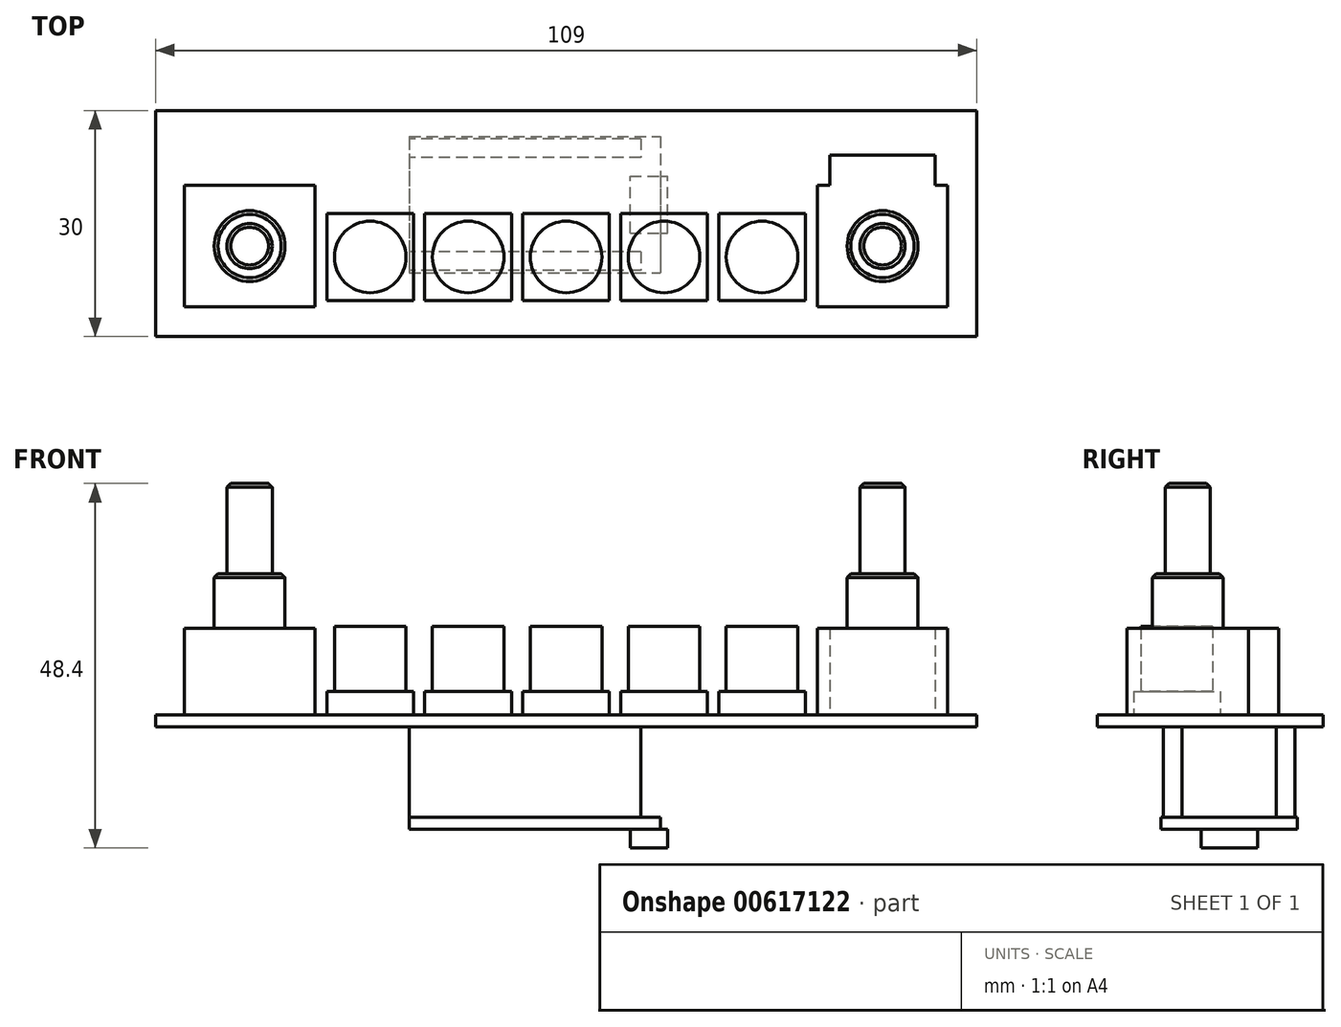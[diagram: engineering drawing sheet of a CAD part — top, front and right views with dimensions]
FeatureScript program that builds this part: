
annotation { "Feature Type Name" : "Feature", "Feature Type Description" : "" }
export const myFeature = defineFeature(function(context is Context, id is Id, definition is map)
    precondition{}
    {
        {
            var Q0;
            Q0=qCreatedBy(makeId("Top.planeOp"),FACE);
            var sketch = newSketch(context, id + "F0", { "sketchPlane" : qUnion([Q0])});
            skLineSegment(sketch, "E0.bottom", {"start": v(54.5, -15) * mm, "end": v(-54.5, -15) * mm});
            skLineSegment(sketch, "E0.top", {"start": v(54.5, 15) * mm, "end": v(-54.5, 15) * mm});
            skLineSegment(sketch, "E0.left", {"start": v(54.5, -15) * mm, "end": v(54.5, 15) * mm});
            skLineSegment(sketch, "E0.right", {"start": v(-54.5, -15) * mm, "end": v(-54.5, 15) * mm});
            skPoint(sketch, "E0.middle", {"position": v(0, 0) * mm});
            skLineSegment(sketch, "E1.bottom", {"start": v(-20.25, -10.2) * mm, "end": v(-31.75, -10.2) * mm});
            skLineSegment(sketch, "E1.top", {"start": v(-20.25, 1.3) * mm, "end": v(-31.75, 1.3) * mm});
            skLineSegment(sketch, "E1.left", {"start": v(-20.25, -10.2) * mm, "end": v(-20.25, 1.3) * mm});
            skLineSegment(sketch, "E1.right", {"start": v(-31.75, -10.2) * mm, "end": v(-31.75, 1.3) * mm});
            skPoint(sketch, "E1.middle", {"position": v(-26, -4.45) * mm});
            skLineSegment(sketch, "E2.1.0.0", {"start": v(-18.75, -10.2) * mm, "end": v(-18.75, 1.3) * mm});
            skLineSegment(sketch, "E2.1.0.1", {"start": v(-7.25, -10.2) * mm, "end": v(-7.25, 1.3) * mm});
            skLineSegment(sketch, "E2.1.0.2", {"start": v(-7.25, 1.3) * mm, "end": v(-18.75, 1.3) * mm});
            skPoint(sketch, "E2.1.0.3", {"position": v(-13, -4.45) * mm});
            skLineSegment(sketch, "E2.1.0.4", {"start": v(-7.25, -10.2) * mm, "end": v(-18.75, -10.2) * mm});
            skLineSegment(sketch, "E2.2.0.0", {"start": v(-5.75, -10.2) * mm, "end": v(-5.75, 1.3) * mm});
            skLineSegment(sketch, "E2.2.0.1", {"start": v(5.75, -10.2) * mm, "end": v(5.75, 1.3) * mm});
            skLineSegment(sketch, "E2.2.0.2", {"start": v(5.75, 1.3) * mm, "end": v(-5.75, 1.3) * mm});
            skPoint(sketch, "E2.2.0.3", {"position": v(0, -4.45) * mm});
            skLineSegment(sketch, "E2.2.0.4", {"start": v(5.75, -10.2) * mm, "end": v(-5.75, -10.2) * mm});
            skLineSegment(sketch, "E2.3.0.0", {"start": v(7.25, -10.2) * mm, "end": v(7.25, 1.3) * mm});
            skLineSegment(sketch, "E2.3.0.1", {"start": v(18.75, -10.2) * mm, "end": v(18.75, 1.3) * mm});
            skLineSegment(sketch, "E2.3.0.2", {"start": v(18.75, 1.3) * mm, "end": v(7.25, 1.3) * mm});
            skPoint(sketch, "E2.3.0.3", {"position": v(13, -4.45) * mm});
            skLineSegment(sketch, "E2.3.0.4", {"start": v(18.75, -10.2) * mm, "end": v(7.25, -10.2) * mm});
            skLineSegment(sketch, "E2.4.0.0", {"start": v(20.25, -10.2) * mm, "end": v(20.25, 1.3) * mm});
            skLineSegment(sketch, "E2.4.0.1", {"start": v(31.75, -10.2) * mm, "end": v(31.75, 1.3) * mm});
            skLineSegment(sketch, "E2.4.0.2", {"start": v(31.75, 1.3) * mm, "end": v(20.25, 1.3) * mm});
            skPoint(sketch, "E2.4.0.3", {"position": v(26, -4.45) * mm});
            skLineSegment(sketch, "E2.4.0.4", {"start": v(31.75, -10.2) * mm, "end": v(20.25, -10.2) * mm});
            skLineSegment(sketch, "E2.direction1", {"start": v(-31.75, -10.2) * mm, "end": v(-18.75, -10.2) * mm, "construction": true});
            skLineSegment(sketch, "E3", {"start": v(0, 21.15) * mm, "end": v(0, -24.83) * mm, "construction": true});
            skSolve(sketch);
        }
        {
            var Q0;
            Q0=makeQuery(id+"F0.imprint","IMPRINT",FACE,{"disambiguationData":[TD([[makeQuery(id+"F0.imprint","IMPRINT",EDGE,{"derivedFrom":sQuery(id+"F0.wireOp",EDGE,"E1.bottom")}),-1.0]])]});
            var Q1;
            Q1=makeQuery(id+"F0.imprint","IMPRINT",FACE,{"disambiguationData":[TD([[makeQuery(id+"F0.imprint","IMPRINT",EDGE,{"derivedFrom":sQuery(id+"F0.wireOp",EDGE,"E2.1.0.0")}),-1.0]])]});
            var Q2;
            Q2=makeQuery(id+"F0.imprint","IMPRINT",FACE,{"disambiguationData":[TD([[makeQuery(id+"F0.imprint","IMPRINT",EDGE,{"derivedFrom":sQuery(id+"F0.wireOp",EDGE,"E2.3.0.0")}),-1.0]])]});
            var Q3;
            Q3=makeQuery(id+"F0.imprint","IMPRINT",FACE,{"disambiguationData":[TD([[makeQuery(id+"F0.imprint","IMPRINT",EDGE,{"derivedFrom":sQuery(id+"F0.wireOp",EDGE,"E2.4.0.0")}),-1.0]])]});
            var Q4;
            Q4=makeQuery(id+"F0.imprint","IMPRINT",FACE,{"disambiguationData":[TD([[makeQuery(id+"F0.imprint","IMPRINT",EDGE,{"derivedFrom":sQuery(id+"F0.wireOp",EDGE,"E2.2.0.0")}),-1.0]])]});
            extrude(context, id + "F1", {"entities" : qUnion([Q0, Q1, Q2, Q3, Q4]), "depth" : 4.7 * mm, "offsetDistance" : 25 * mm});
        }
        {
            var Q0;
            Q0=makeQuery(id+"F0.imprint","IMPRINT",FACE,{"disambiguationData":[TD([[makeQuery(id+"F0.imprint","IMPRINT",EDGE,{"derivedFrom":sQuery(id+"F0.wireOp",EDGE,"E0.bottom")}),-1.0]])]});
            extrude(context, id + "F2", {"entities" : qUnion([Q0]), "operationType" : NewBodyOperationType.ADD, "depth" : 1.6 * mm, "offsetDistance" : 25 * mm});
        }
        {
            var Q0;
            Q0=makeQuery(id+"F1.opExtrude","CAP_FACE",FACE,{"disambiguationData":[OSD([sQuery(id+"F0.wireOp",EDGE,"E1.bottom"),sQuery(id+"F0.wireOp",EDGE,"E1.top"),sQuery(id+"F0.wireOp",EDGE,"E1.left"),sQuery(id+"F0.wireOp",EDGE,"E1.right")])],"isStart":false});
            var sketch = newSketch(context, id + "F3", { "sketchPlane" : qUnion([Q0])});
            skCircle(sketch, "E4", {"center": v(-26, -4.45) * mm, "radius": 4.75 * mm});
            skCircle(sketch, "E5.1.0.0", {"center": v(-13, -4.45) * mm, "radius": 4.75 * mm});
            skCircle(sketch, "E5.2.0.0", {"center": v(0, -4.45) * mm, "radius": 4.75 * mm});
            skCircle(sketch, "E5.3.0.0", {"center": v(13, -4.45) * mm, "radius": 4.75 * mm});
            skCircle(sketch, "E5.4.0.0", {"center": v(26, -4.45) * mm, "radius": 4.75 * mm});
            skLineSegment(sketch, "E5.direction1", {"start": v(-26, -4.45) * mm, "end": v(-13, -4.45) * mm, "construction": true});
            skSolve(sketch);
        }
        {
            var Q0;
            Q0=makeQuery(id+"F3.imprint","IMPRINT",FACE,{"disambiguationData":[TD([[makeQuery(id+"F3.imprint","IMPRINT",EDGE,{"derivedFrom":sQuery(id+"F3.wireOp",EDGE,"E4")}),1.0]])]});
            var Q1;
            Q1=makeQuery(id+"F3.imprint","IMPRINT",FACE,{"disambiguationData":[TD([[makeQuery(id+"F3.imprint","IMPRINT",EDGE,{"derivedFrom":sQuery(id+"F3.wireOp",EDGE,"E5.1.0.0")}),1.0]])]});
            var Q2;
            Q2=makeQuery(id+"F3.imprint","IMPRINT",FACE,{"disambiguationData":[TD([[makeQuery(id+"F3.imprint","IMPRINT",EDGE,{"derivedFrom":sQuery(id+"F3.wireOp",EDGE,"E5.2.0.0")}),1.0]])]});
            var Q3;
            Q3=makeQuery(id+"F3.imprint","IMPRINT",FACE,{"disambiguationData":[TD([[makeQuery(id+"F3.imprint","IMPRINT",EDGE,{"derivedFrom":sQuery(id+"F3.wireOp",EDGE,"E5.3.0.0")}),1.0]])]});
            var Q4;
            Q4=makeQuery(id+"F3.imprint","IMPRINT",FACE,{"disambiguationData":[TD([[makeQuery(id+"F3.imprint","IMPRINT",EDGE,{"derivedFrom":sQuery(id+"F3.wireOp",EDGE,"E5.4.0.0")}),1.0]])]});
            extrude(context, id + "F4", {"entities" : qUnion([Q0, Q1, Q2, Q3, Q4]), "operationType" : NewBodyOperationType.ADD, "depth" : 8.6 * mm, "offsetDistance" : 25 * mm});
        }
        {
            var Q0;
            Q0=makeQuery(id+"F2.opExtrude","CAP_FACE",FACE,{"disambiguationData":[OSD([sQuery(id+"F0.wireOp",EDGE,"E0.bottom"),sQuery(id+"F0.wireOp",EDGE,"E0.top"),sQuery(id+"F0.wireOp",EDGE,"E0.left"),sQuery(id+"F0.wireOp",EDGE,"E0.right"),sQuery(id+"F0.wireOp",EDGE,"E1.bottom"),sQuery(id+"F0.wireOp",EDGE,"E1.top"),sQuery(id+"F0.wireOp",EDGE,"E1.left"),sQuery(id+"F0.wireOp",EDGE,"E1.right"),sQuery(id+"F0.wireOp",EDGE,"E2.1.0.0"),sQuery(id+"F0.wireOp",EDGE,"E2.1.0.1"),sQuery(id+"F0.wireOp",EDGE,"E2.1.0.2"),sQuery(id+"F0.wireOp",EDGE,"E2.1.0.4"),sQuery(id+"F0.wireOp",EDGE,"E2.2.0.0"),sQuery(id+"F0.wireOp",EDGE,"E2.2.0.1"),sQuery(id+"F0.wireOp",EDGE,"E2.2.0.2"),sQuery(id+"F0.wireOp",EDGE,"E2.2.0.4"),sQuery(id+"F0.wireOp",EDGE,"E2.3.0.0"),sQuery(id+"F0.wireOp",EDGE,"E2.3.0.1"),sQuery(id+"F0.wireOp",EDGE,"E2.3.0.2"),sQuery(id+"F0.wireOp",EDGE,"E2.3.0.4"),sQuery(id+"F0.wireOp",EDGE,"E2.4.0.0"),sQuery(id+"F0.wireOp",EDGE,"E2.4.0.1"),sQuery(id+"F0.wireOp",EDGE,"E2.4.0.2"),sQuery(id+"F0.wireOp",EDGE,"E2.4.0.4")])],"isStart":false});
            var sketch = newSketch(context, id + "F5", { "sketchPlane" : qUnion([Q0])});
            skLineSegment(sketch, "E6.bottom", {"start": v(-33.35, -11.05) * mm, "end": v(-50.65, -11.05) * mm});
            skLineSegment(sketch, "E6.top", {"start": v(-33.35, 5.05) * mm, "end": v(-50.65, 5.05) * mm});
            skLineSegment(sketch, "E6.left", {"start": v(-33.35, -11.05) * mm, "end": v(-33.35, 5.05) * mm});
            skLineSegment(sketch, "E6.right", {"start": v(-50.65, -11.05) * mm, "end": v(-50.65, 5.05) * mm});
            skPoint(sketch, "E6.middle", {"position": v(-42, -3) * mm});
            skLineSegment(sketch, "E7.bottom", {"start": v(-35, 5.05) * mm, "end": v(-49, 5.05) * mm});
            skLineSegment(sketch, "E7.top", {"start": v(-35, 9.05) * mm, "end": v(-49, 9.05) * mm});
            skLineSegment(sketch, "E7.left", {"start": v(-35, 5.05) * mm, "end": v(-35, 9.05) * mm});
            skLineSegment(sketch, "E7.right", {"start": v(-49, 5.05) * mm, "end": v(-49, 9.05) * mm});
            skPoint(sketch, "E7.middle", {"position": v(-42, 7.05) * mm});
            skLineSegment(sketch, "E8", {"start": v(-39.97, -18.43) * mm, "end": v(-39.97, -18.43) * mm});
            skLineSegment(sketch, "E9", {"start": v(-42, -34.93) * mm, "end": v(-42, 23.71) * mm, "construction": true});
            skPoint(sketch, "E10.1.0.0", {"position": v(42, 7.05) * mm});
            skLineSegment(sketch, "E10.1.0.1", {"start": v(50.65, -11.05) * mm, "end": v(33.35, -11.05) * mm});
            skLineSegment(sketch, "E10.1.0.2", {"start": v(49, 9.05) * mm, "end": v(35, 9.05) * mm});
            skLineSegment(sketch, "E10.1.0.3", {"start": v(50.65, -11.05) * mm, "end": v(50.65, 5.05) * mm});
            skPoint(sketch, "E10.1.0.4", {"position": v(42, -3) * mm});
            skLineSegment(sketch, "E10.1.0.5", {"start": v(33.35, -11.05) * mm, "end": v(33.35, 5.05) * mm});
            skLineSegment(sketch, "E10.1.0.6", {"start": v(49, 5.05) * mm, "end": v(35, 5.05) * mm});
            skLineSegment(sketch, "E10.1.0.7", {"start": v(50.65, 5.05) * mm, "end": v(33.35, 5.05) * mm});
            skLineSegment(sketch, "E10.1.0.8", {"start": v(35, 5.05) * mm, "end": v(35, 9.05) * mm});
            skLineSegment(sketch, "E10.1.0.9", {"start": v(49, 5.05) * mm, "end": v(49, 9.05) * mm});
            skLineSegment(sketch, "E10.direction1", {"start": v(-50.65, -11.05) * mm, "end": v(33.35, -11.05) * mm, "construction": true});
            skSolve(sketch);
        }
        {
            var Q0;
            Q0=makeQuery(id+"F5.imprint","IMPRINT",FACE,{"disambiguationData":[TD([[makeQuery(id+"F5.imprint","IMPRINT",EDGE,{"derivedFrom":sQuery(id+"F5.wireOp",EDGE,"E6.bottom")}),-1.0]])]});
            var Q1;
            Q1=makeQuery(id+"F5.imprint","IMPRINT",FACE,{"disambiguationData":[TD([[makeQuery(id+"F5.imprint","IMPRINT",EDGE,{"derivedFrom":sQuery(id+"F5.wireOp",EDGE,"E7.bottom")}),-1.0]])]});
            var Q2;
            Q2=makeQuery(id+"F5.imprint","IMPRINT",FACE,{"disambiguationData":[TD([[makeQuery(id+"F5.imprint","IMPRINT",EDGE,{"derivedFrom":sQuery(id+"F5.wireOp",EDGE,"E10.1.0.2")}),1.0]])]});
            var Q3;
            Q3=makeQuery(id+"F5.imprint","IMPRINT",FACE,{"disambiguationData":[TD([[makeQuery(id+"F5.imprint","IMPRINT",EDGE,{"derivedFrom":sQuery(id+"F5.wireOp",EDGE,"E10.1.0.1")}),-1.0]])]});
            extrude(context, id + "F6", {"entities" : qUnion([Q0, Q1, Q2, Q3]), "operationType" : NewBodyOperationType.ADD, "depth" : 11.5 * mm, "offsetDistance" : 25 * mm});
        }
        {
            var Q0;
            Q0=makeQuery(id+"F6.opExtrude","CAP_FACE",FACE,{"disambiguationData":[OSD([sQuery(id+"F5.wireOp",EDGE,"E6.bottom"),sQuery(id+"F5.wireOp",EDGE,"E6.top"),sQuery(id+"F5.wireOp",EDGE,"E6.left"),sQuery(id+"F5.wireOp",EDGE,"E6.right"),sQuery(id+"F5.wireOp",EDGE,"E7.top"),sQuery(id+"F5.wireOp",EDGE,"E7.left"),sQuery(id+"F5.wireOp",EDGE,"E7.right")])],"isStart":false});
            var sketch = newSketch(context, id + "F7", { "sketchPlane" : qUnion([Q0])});
            skCircle(sketch, "E11", {"center": v(-42, -3) * mm, "radius": 4.7 * mm});
            skLineSegment(sketch, "E12", {"start": v(-50.65, -11.05) * mm, "end": v(-33.35, 5.05) * mm, "construction": true});
            skLineSegment(sketch, "E13", {"start": v(-50.65, 5.05) * mm, "end": v(-33.35, -11.05) * mm, "construction": true});
            skCircle(sketch, "E14.1.0.0", {"center": v(42, -3) * mm, "radius": 4.7 * mm});
            skLineSegment(sketch, "E14.direction1", {"start": v(-42, -3) * mm, "end": v(42, -3) * mm, "construction": true});
            skSolve(sketch);
        }
        {
            var Q0;
            Q0=makeQuery(id+"F7.imprint","IMPRINT",FACE,{"disambiguationData":[TD([[makeQuery(id+"F7.imprint","IMPRINT",EDGE,{"derivedFrom":sQuery(id+"F7.wireOp",EDGE,"E11")}),1.0]])]});
            var Q1;
            Q1=makeQuery(id+"F7.imprint","IMPRINT",FACE,{"disambiguationData":[TD([[makeQuery(id+"F7.imprint","IMPRINT",EDGE,{"derivedFrom":sQuery(id+"F7.wireOp",EDGE,"E14.1.0.0")}),1.0]])]});
            extrude(context, id + "F8", {"entities" : qUnion([Q0, Q1]), "operationType" : NewBodyOperationType.ADD, "depth" : 7.2 * mm, "offsetDistance" : 25 * mm});
        }
        {
            var Q0;
            Q0=makeQuery(id+"F8.opExtrude","CAP_FACE",FACE,{"disambiguationData":[OSD([sQuery(id+"F7.wireOp",EDGE,"E11")])],"isStart":false});
            var sketch = newSketch(context, id + "F9", { "sketchPlane" : qUnion([Q0])});
            skCircle(sketch, "E15", {"center": v(-42, -3) * mm, "radius": 3 * mm});
            skCircle(sketch, "E16.1.0.0", {"center": v(42, -3) * mm, "radius": 3 * mm});
            skLineSegment(sketch, "E16.direction1", {"start": v(-42, -3) * mm, "end": v(42, -3) * mm, "construction": true});
            skSolve(sketch);
        }
        {
            var Q0;
            Q0=makeQuery(id+"F9.imprint","IMPRINT",FACE,{"disambiguationData":[TD([[makeQuery(id+"F9.imprint","IMPRINT",EDGE,{"derivedFrom":sQuery(id+"F9.wireOp",EDGE,"E15")}),1.0]])]});
            var Q1;
            Q1=makeQuery(id+"F9.imprint","IMPRINT",FACE,{"disambiguationData":[TD([[makeQuery(id+"F9.imprint","IMPRINT",EDGE,{"derivedFrom":sQuery(id+"F9.wireOp",EDGE,"E16.1.0.0")}),1.0]])]});
            extrude(context, id + "F10", {"entities" : qUnion([Q0, Q1]), "operationType" : NewBodyOperationType.ADD, "depth" : 12 * mm, "offsetDistance" : 25 * mm});
        }
        {
            var Q0;
            Q0=makeQuery(id+"F8.opExtrude","CAP_EDGE",EDGE,{"disambiguationData":[OSD([sQuery(id+"F7.wireOp",EDGE,"E11")])],"isStart":false});
            var Q1;
            Q1=makeQuery(id+"F8.opExtrude","CAP_EDGE",EDGE,{"disambiguationData":[OSD([sQuery(id+"F7.wireOp",EDGE,"E14.1.0.0")])],"isStart":false});
            var Q2;
            Q2=makeQuery(id+"F10.opExtrude","CAP_EDGE",EDGE,{"disambiguationData":[OSD([sQuery(id+"F9.wireOp",EDGE,"E15")])],"isStart":false});
            var Q3;
            Q3=makeQuery(id+"F10.opExtrude","CAP_EDGE",EDGE,{"disambiguationData":[OSD([sQuery(id+"F9.wireOp",EDGE,"E16.1.0.0")])],"isStart":false});
            chamfer(context, id + "F11", {"entities" : qUnion([Q0, Q1, Q2, Q3]), "width" : 0.5 * mm, "tangentPropagation" : true});
        }
        {
            var Q0;
            Q0=makeQuery(id+"F0.imprint","IMPRINT",FACE,{"disambiguationData":[TD([[makeQuery(id+"F0.imprint","IMPRINT",EDGE,{"derivedFrom":sQuery(id+"F0.wireOp",EDGE,"E0.bottom")}),-1.0]])]});
            var sketch = newSketch(context, id + "F12", { "sketchPlane" : qUnion([Q0])});
            skLineSegment(sketch, "E17.bottom", {"start": v(9.9, 11.25) * mm, "end": v(-20.8, 11.25) * mm});
            skLineSegment(sketch, "E17.top", {"start": v(9.9, 8.75) * mm, "end": v(-20.8, 8.75) * mm});
            skLineSegment(sketch, "E17.left", {"start": v(9.9, 11.25) * mm, "end": v(9.9, 8.75) * mm});
            skLineSegment(sketch, "E17.right", {"start": v(-20.8, 11.25) * mm, "end": v(-20.8, 8.75) * mm});
            skPoint(sketch, "E17.middle", {"position": v(-5.45, 10) * mm});
            skLineSegment(sketch, "E18.bottom", {"start": v(9.9, -3.75) * mm, "end": v(-20.8, -3.75) * mm});
            skLineSegment(sketch, "E18.top", {"start": v(9.9, -6.25) * mm, "end": v(-20.8, -6.25) * mm});
            skLineSegment(sketch, "E18.left", {"start": v(9.9, -3.75) * mm, "end": v(9.9, -6.25) * mm});
            skLineSegment(sketch, "E18.right", {"start": v(-20.8, -3.75) * mm, "end": v(-20.8, -6.25) * mm});
            skPoint(sketch, "E18.middle", {"position": v(-5.45, -5) * mm});
            skSolve(sketch);
        }
        {
            var Q0;
            {var subQ0=sQuery(id+"F12.wireOp",EDGE,"E18.bottom");var subQ1=makeQuery(id+"F0.imprint","IMPRINT",EDGE,{"derivedFrom":sQuery(id+"F0.wireOp",EDGE,"E2.1.0.0")});var subQ2=makeQuery(id+"F12.imprint","INTERSECT",VERTEX,{"derivedFrom":[subQ1,subQ0]});Q0=makeQuery(id+"F12.imprint","IMPRINT",FACE,{"disambiguationData":[TD([[makeQuery(id+"F12.imprint","IMPRINT",EDGE,{"disambiguationData":[TD([[subQ2,-1.0]])],"derivedFrom":subQ0}),1.0]])]});}
            var Q1;
            {var subQ0=sQuery(id+"F12.wireOp",EDGE,"E18.bottom");var subQ1=makeQuery(id+"F0.imprint","IMPRINT",EDGE,{"derivedFrom":sQuery(id+"F0.wireOp",EDGE,"E2.1.0.1")});var subQ2=makeQuery(id+"F12.imprint","INTERSECT",VERTEX,{"derivedFrom":[subQ1,subQ0]});Q1=makeQuery(id+"F12.imprint","IMPRINT",FACE,{"disambiguationData":[TD([[makeQuery(id+"F12.imprint","IMPRINT",EDGE,{"disambiguationData":[TD([[subQ2,-1.0]])],"derivedFrom":subQ0}),1.0]])]});}
            var Q2;
            {var subQ0=sQuery(id+"F12.wireOp",EDGE,"E18.bottom");var subQ1=makeQuery(id+"F0.imprint","IMPRINT",EDGE,{"derivedFrom":sQuery(id+"F0.wireOp",EDGE,"E2.2.0.0")});var subQ2=makeQuery(id+"F12.imprint","INTERSECT",VERTEX,{"derivedFrom":[subQ1,subQ0]});Q2=makeQuery(id+"F12.imprint","IMPRINT",FACE,{"disambiguationData":[TD([[makeQuery(id+"F12.imprint","IMPRINT",EDGE,{"disambiguationData":[TD([[subQ2,-1.0]])],"derivedFrom":subQ0}),1.0]])]});}
            var Q3;
            {var subQ0=sQuery(id+"F12.wireOp",EDGE,"E18.bottom");var subQ1=makeQuery(id+"F0.imprint","IMPRINT",EDGE,{"derivedFrom":sQuery(id+"F0.wireOp",EDGE,"E2.2.0.1")});var subQ2=makeQuery(id+"F12.imprint","INTERSECT",VERTEX,{"derivedFrom":[subQ1,subQ0]});Q3=makeQuery(id+"F12.imprint","IMPRINT",FACE,{"disambiguationData":[TD([[makeQuery(id+"F12.imprint","IMPRINT",EDGE,{"disambiguationData":[TD([[subQ2,-1.0]])],"derivedFrom":subQ0}),1.0]])]});}
            var Q4;
            {var subQ0=sQuery(id+"F12.wireOp",EDGE,"E18.bottom");var subQ1=makeQuery(id+"F0.imprint","IMPRINT",EDGE,{"derivedFrom":sQuery(id+"F0.wireOp",EDGE,"E2.3.0.0")});var subQ2=makeQuery(id+"F12.imprint","INTERSECT",VERTEX,{"derivedFrom":[subQ1,subQ0]});Q4=makeQuery(id+"F12.imprint","IMPRINT",FACE,{"disambiguationData":[TD([[makeQuery(id+"F12.imprint","IMPRINT",EDGE,{"disambiguationData":[TD([[subQ2,-1.0]])],"derivedFrom":subQ0}),1.0]])]});}
            var Q5;
            {var subQ0=sQuery(id+"F12.wireOp",EDGE,"E18.left");Q5=makeQuery(id+"F12.imprint","IMPRINT",FACE,{"disambiguationData":[TD([[makeQuery(id+"F12.imprint","IMPRINT",EDGE,{"derivedFrom":subQ0}),-1.0]])]});}
            var Q6;
            {var subQ0=sQuery(id+"F12.wireOp",EDGE,"E18.right");Q6=makeQuery(id+"F12.imprint","IMPRINT",FACE,{"disambiguationData":[TD([[makeQuery(id+"F12.imprint","IMPRINT",EDGE,{"derivedFrom":subQ0}),1.0]])]});}
            var Q7;
            Q7=makeQuery(id+"F12.imprint","IMPRINT",FACE,{"disambiguationData":[TD([[makeQuery(id+"F12.imprint","IMPRINT",EDGE,{"derivedFrom":sQuery(id+"F12.wireOp",EDGE,"E17.bottom")}),1.0]])]});
            extrude(context, id + "F13", {"entities" : qUnion([Q0, Q1, Q2, Q3, Q4, Q5, Q6, Q7]), "operationType" : NewBodyOperationType.ADD, "oppositeDirection" : true, "depth" : 12 * mm, "offsetDistance" : 25 * mm});
        }
        {
            var Q0;
            Q0=makeQuery(id+"F13.opExtrude","CAP_FACE",FACE,{"disambiguationData":[OSD([sQuery(id+"F12.wireOp",EDGE,"E17.bottom"),sQuery(id+"F12.wireOp",EDGE,"E17.top"),sQuery(id+"F12.wireOp",EDGE,"E17.left"),sQuery(id+"F12.wireOp",EDGE,"E17.right")])],"isStart":false});
            var sketch = newSketch(context, id + "F14", { "sketchPlane" : qUnion([Q0])});
            skLineSegment(sketch, "E19.bottom", {"start": v(-20.8, -11.55) * mm, "end": v(12.5, -11.55) * mm});
            skLineSegment(sketch, "E19.top", {"start": v(-20.8, 6.55) * mm, "end": v(12.5, 6.55) * mm});
            skLineSegment(sketch, "E19.left", {"start": v(-20.8, -11.55) * mm, "end": v(-20.8, 6.55) * mm});
            skLineSegment(sketch, "E19.right", {"start": v(12.5, -11.55) * mm, "end": v(12.5, 6.55) * mm});
            skSolve(sketch);
        }
        {
            var Q0;
            {var subQ4=sQuery(id+"F14.wireOp",EDGE,"E19.bottom");Q0=makeQuery(id+"F14.imprint","IMPRINT",FACE,{"disambiguationData":[TD([[makeQuery(id+"F14.imprint","IMPRINT",EDGE,{"derivedFrom":subQ4}),1.0]])]});}
            var Q1;
            {var subQ1=makeQuery(id+"F13.opExtrude","CAP_EDGE",EDGE,{"disambiguationData":[OSD([sQuery(id+"F12.wireOp",EDGE,"E17.bottom")])],"isStart":false});Q1=makeQuery(id+"F14.imprint","IMPRINT",FACE,{"disambiguationData":[TD([[makeQuery(id+"F14.imprint","IMPRINT",EDGE,{"derivedFrom":subQ1}),-1.0]])]});}
            extrude(context, id + "F15", {"entities" : qUnion([Q0, Q1]), "operationType" : NewBodyOperationType.ADD, "depth" : 1.6 * mm, "offsetDistance" : 25 * mm});
        }
        {
            var Q0;
            Q0=makeQuery(id+"F15.opExtrude","CAP_FACE",FACE,{"disambiguationData":[OSD([sQuery(id+"F14.wireOp",EDGE,"E19.bottom"),sQuery(id+"F14.wireOp",EDGE,"E19.top"),sQuery(id+"F14.wireOp",EDGE,"E19.left"),sQuery(id+"F14.wireOp",EDGE,"E19.right")])],"isStart":false});
            var sketch = newSketch(context, id + "F16", { "sketchPlane" : qUnion([Q0])});
            skLineSegment(sketch, "E20.bottom", {"start": v(8.5, 1.25) * mm, "end": v(13.5, 1.25) * mm});
            skLineSegment(sketch, "E20.top", {"start": v(8.5, -6.25) * mm, "end": v(13.5, -6.25) * mm});
            skLineSegment(sketch, "E20.left", {"start": v(8.5, 1.25) * mm, "end": v(8.5, -6.25) * mm});
            skLineSegment(sketch, "E20.right", {"start": v(13.5, 1.25) * mm, "end": v(13.5, -6.25) * mm});
            skSolve(sketch);
        }
        {
            var Q0;
            {var subQ0=sQuery(id+"F16.wireOp",EDGE,"E20.left");Q0=makeQuery(id+"F16.imprint","IMPRINT",FACE,{"disambiguationData":[TD([[makeQuery(id+"F16.imprint","IMPRINT",EDGE,{"derivedFrom":subQ0}),1.0]])]});}
            var Q1;
            {var subQ0=sQuery(id+"F16.wireOp",EDGE,"E20.right");Q1=makeQuery(id+"F16.imprint","IMPRINT",FACE,{"disambiguationData":[TD([[makeQuery(id+"F16.imprint","IMPRINT",EDGE,{"derivedFrom":subQ0}),-1.0]])]});}
            extrude(context, id + "F17", {"entities" : qUnion([Q0, Q1]), "operationType" : NewBodyOperationType.ADD, "depth" : 2.5 * mm, "offsetDistance" : 25 * mm});
        }
    });
